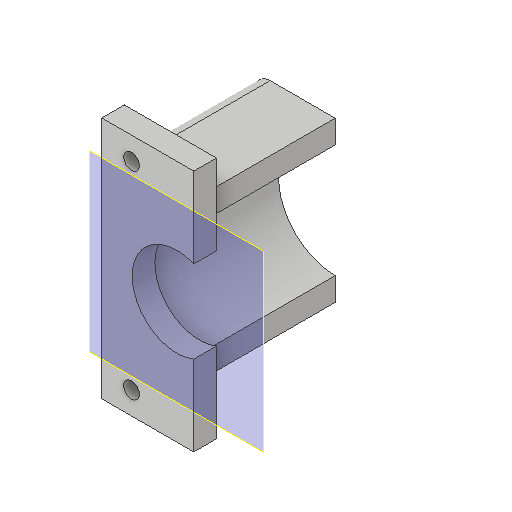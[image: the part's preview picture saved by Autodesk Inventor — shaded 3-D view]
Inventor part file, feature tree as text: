
AUTODESK INVENTOR PART (.ipt)
format: ipt  version: 2022 (Build 260153000, 153)  size: 169,984 bytes
history: native  units: mm
features: reference x5, other x5, extrude x3, plane x2, sketch x2, projected_geometry x1
ambient origin geometry x8: Origin, YZ Plane, XZ Plane, XY Plane, X Axis, Y Axis, Z Axis, Center Point
bodies: Body1 (feature_tree)
feature tree (18):
  plane  "Work Plane3"
  extrude  "Extrusion2"  Depth=4.0mm
  sketch  "Sketch3"  dims[d9=4.0mm d10=0.0mm d11=20.0mm]
  plane  "Work Plane4"
  extrude  "Extrusion3"  Depth=15.0mm TaperAngle=0.0deg
  extrude  "Extrusion4"  Depth=4.0mm
  projected_geometry  "Projected Loop1"
  sketch  "Sketch4"  dims[d12=24.0mm d13=0.0mm d14=15.0mm d15=0.0mm d16=2.8mm d17=2.8mm d26=2.8mm d27=2.8mm d28=4.0mm d29=4.0mm d30=11.0mm]
  reference  "Reference15"
  reference  "Reference16"
  reference  "Reference17"
  reference  "Reference18"
  reference  "Reference19"
  other  "Assembly_Cube_Z_Focus_MGN_NEMA_v3.iam"
  other  "00_Stepper_Motor_28BYJ-48:1"
  other  "00_NEMA11:1"
  other  "Assembly_Motorcoupling_Nema_M3_Selfcentering:1"
  other  "00_coupler_5_3_nema_screw:1"
